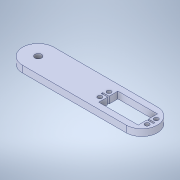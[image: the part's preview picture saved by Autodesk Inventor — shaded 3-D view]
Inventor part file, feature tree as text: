
AUTODESK INVENTOR PART (.ipt)
format: ipt  version: 2020 (Build 240168000, 168)  size: 157,184 bytes
history: mixed  units: mm
features: other x3, extrude x1, sketch x1, imported_body x1
ambient origin geometry x8: Origin, YZ Plane, XZ Plane, XY Plane, X Axis, Y Axis, Z Axis, Center Point
bodies: Body1 (imported_parasolid)
feature tree (6):
  other  "Твердое тело1"
  other  "РабПлоскость1"
  extrude  "Выдавливание1"  Depth=10.0mm TaperAngle=0.0deg
  sketch  "Эскиз1"
  other  "Saliente-Extruir3"
  imported_body  NMx_Import_Brep_tag  [imported B-rep: ~23 faces, bbox_mm=[120.283253, 7.0, 32.5]]
